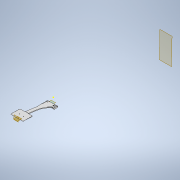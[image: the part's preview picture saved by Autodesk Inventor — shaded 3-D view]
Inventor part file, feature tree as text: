
AUTODESK INVENTOR PART (.ipt)
format: ipt  version: 2022 (Build 260153000, 153)  size: 547,328 bytes
history: native  units: in
note: dims shown in document units (in); Inventor stores cm internally (conversion verified against a paired STEP export)
features: extrude x19, sketch x19, projected_geometry x15, plane x6, fillet x6, sweep x1
ambient origin geometry x8: Origin, YZ Plane, XZ Plane, XY Plane, X Axis, Y Axis, Z Axis, Center Point
bodies: Solid1 (feature_tree)
feature tree (66):
  extrude  "Extrusion1"  Depth=2.2in
  extrude  "Extrusion2"  Depth=0.125in
  extrude  "Extrusion3"  Depth=1.0in TaperAngle=0.0deg
  extrude  "Extrusion4"  Depth=0.12in
  sketch  "Sketch5"  dims[d14=0.4in d15=0.12in]
  plane  "Work Plane1"
  sweep  "Sweep2"
  extrude  "Extrusion5"  Depth=0.4in
  plane  "Work Plane6"
  extrude  "Extrusion6"  Depth=0.0625in
  plane  "Work Plane2"
  plane  "Work Plane3"
  plane  "Work Plane4"
  plane  "Work Plane5"
  extrude  "Extrusion7"  Depth=0.125in
  extrude  "Extrusion8"  Depth=0.125in
  extrude  "Extrusion9"  TaperAngle=0.0deg  [1 undecoded]
  sketch  "Sketch12"  dims[d36=2.1in d37=1.05in]
  extrude  "Extrusion10"  Depth=1.0in TaperAngle=0.0deg
  extrude  "Extrusion11"  Depth=1.05in
  extrude  "Extrusion12"  Depth=2.8in
  sketch  "Sketch13"  dims[d38=1.0in d39=0.0in d40=2.8in]
  extrude  "Extrusion13"  Depth=0.1in TaperAngle=0.0deg
  extrude  "Extrusion14"  Depth=0.125in
  fillet  "Fillet2"  Radius=1.0in
  fillet  "Fillet3"  Radius=0.12in
  fillet  "Fillet4"  Radius=0.12in
  fillet  "Fillet5"  [1 undecoded]
  extrude  "Extrusion15"  Depth=0.4in
  extrude  "Extrusion16"  Depth=0.12in
  extrude  "Extrusion17"  Depth=1.0in TaperAngle=0.0deg
  fillet  "Fillet6"  Radius=1.0in
  sketch  "Sketch19"  dims[d63=0.125in d64=0.125in d65=0.125in d66=0.125in d67=0.2in d68=1.0in d69=0.0in d70=0.5in d71=0.3in d72=0.12in d73=0.12in d74=1.0in d75=0.0in d76=3.5in d77=0.0in d78=0.125in d79=0.125in d80=1.25in d81=1.25in d82=1.0in d83=0.0in d84=1.0in d85=0.0in d86=0.125in]
  extrude  "Extrusion18"  Depth=0.125in
  extrude  "Extrusion19"  Depth=0.125in
  fillet  "Fillet7"  Radius=0.125in
  sketch  "Sketch1"  dims[d1=2.5in d2=2.2in]
  sketch  "Sketch2"  dims[d3=0.825in d4=0.0in d5=0.125in]
  projected_geometry  "Projected Loop1"
  sketch  "Sketch3"  dims[d6=0.7in d7=0.0in d8=1.0in d9=0.0in]
  projected_geometry  "Projected Loop2"
  sketch  "Sketch4"  dims[d11=0.4in d13=0.12in]
  sketch  "Sketch6"  dims[d16=1.0in d17=0.0in d18=0.4in]
  sketch  "Sketch7"  dims[d19=30.0in d22=0.0625in]
  projected_geometry  "Projected Loop3"
  sketch  "Sketch8"  dims[d23=0.125in d26=0.0625in]
  projected_geometry  "Projected Loop4"
  sketch  "Sketch9"  dims[d27=0.3in d28=0.125in]
  sketch  "Sketch10"  dims[d29=0.6in d30=0.0in d31=0.0in]
  projected_geometry  "Projected Loop5"
  projected_geometry  "Projected Loop6"
  projected_geometry  "Projected Loop7"
  sketch  "Sketch11"  dims[d32=1.0in d33=0.0in d34=1.0in d35=0.0in]
  projected_geometry  "Projected Loop8"
  projected_geometry  "Projected Loop9"
  sketch  "Sketch14"  dims[d41=1.0in d42=0.0in d43=0.1in d44=0.0in]
  projected_geometry  "Projected Loop10"
  sketch  "Sketch15"  dims[d45=0.8in d46=0.125in d47=1.0in d48=0.0in d49=0.12in d50=0.12in d51=0.0in d52=0.0in]
  projected_geometry  "Projected Loop11"
  sketch  "Sketch16"  dims[d53=1.0in d54=0.0in d55=0.4in]
  projected_geometry  "Projected Loop12"
  sketch  "Sketch17"  dims[d56=0.8in d57=0.12in]
  sketch  "Sketch18"  dims[d58=0.12in d59=1.0in d60=0.0in d61=1.0in d62=0.0in]
  projected_geometry  "Projected Loop13"
  projected_geometry  "Projected Loop14"
  projected_geometry  "Projected Loop15"
note: 2 required parameter values undecoded (feature->parameter linkage not recoverable at this tier; creation-order binding heuristic only, values carry confidence <= 0.55)
